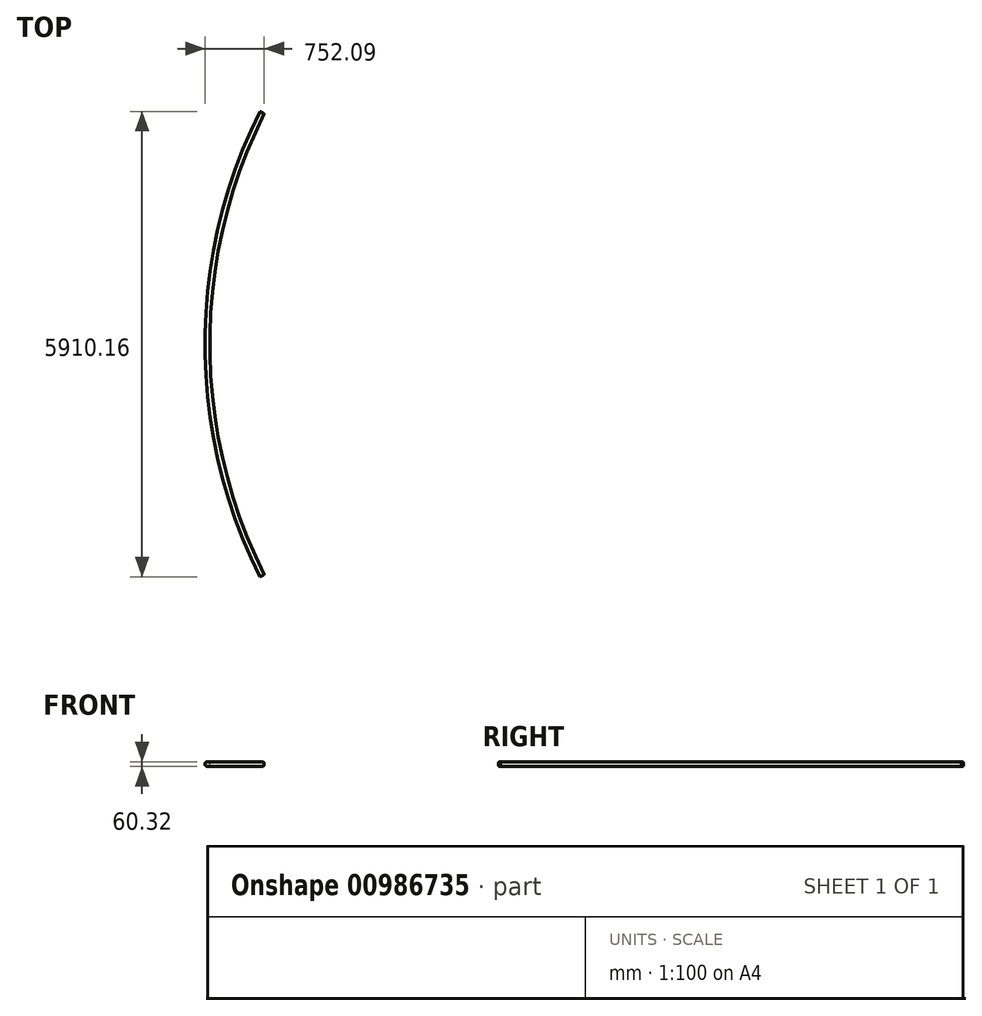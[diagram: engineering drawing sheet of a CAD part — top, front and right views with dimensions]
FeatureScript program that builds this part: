
annotation { "Feature Type Name" : "Feature", "Feature Type Description" : "" }
export const myFeature = defineFeature(function(context is Context, id is Id, definition is map)
    precondition{}
    {
        {
            var Q0;
            Q0=qCreatedBy(makeId("Front.planeOp"),FACE);
            var sketch = newSketch(context, id + "F0", { "sketchPlane" : qUnion([Q0])});
            skCircle(sketch, "E0", {"center": v(0, 0) * mm, "radius": 30.16 * mm});
            skLineSegment(sketch, "E1", {"start": v(0, 0) * mm, "end": v(6573, 0) * mm, "construction": true});
            skLineSegment(sketch, "E2", {"start": v(6573, 0) * mm, "end": v(6573, -100) * mm, "construction": true});
            skCircle(sketch, "E3.0", {"center": v(0, 0) * mm, "radius": 27.4 * mm});
            skSolve(sketch);
        }
        {
            var Q0;
            Q0=qSketchRegion(id+"F0",true);
            var Q1;
            Q1=sQuery(id+"F0.wireOp",EDGE,"E2");
            revolve(context, id + "F1", {"surfaceOperationType" : NewSurfaceOperationType.NEW, "entities" : qUnion([Q0]), "axis" : qUnion([Q1]), "revolveType" : RevolveType.SYMMETRIC, "angle" : 53.17 * degree});
        }
    });
